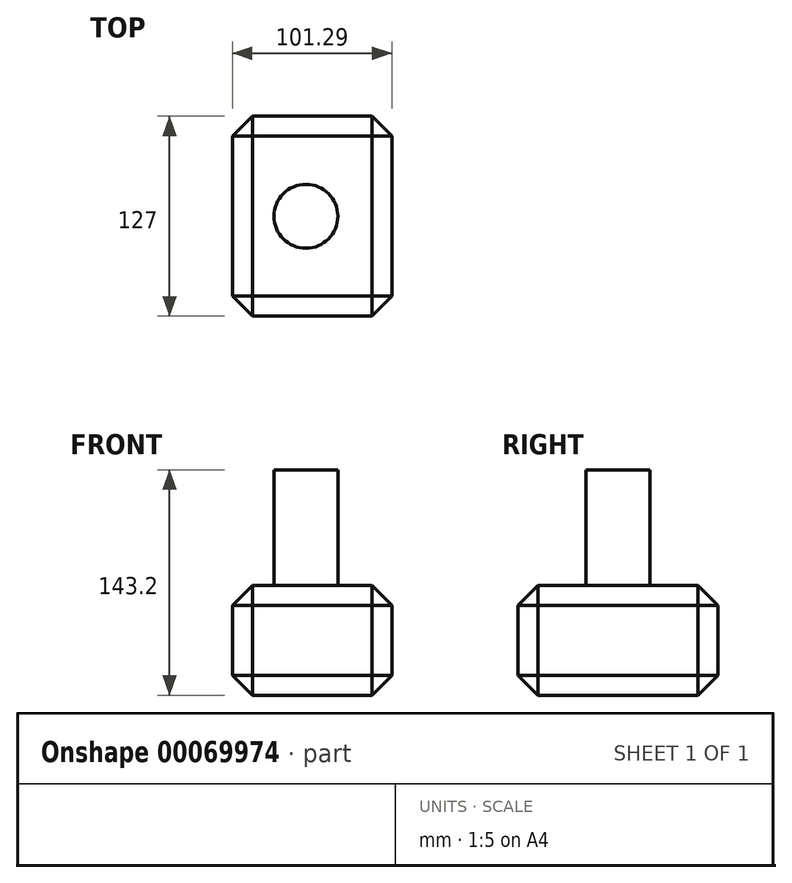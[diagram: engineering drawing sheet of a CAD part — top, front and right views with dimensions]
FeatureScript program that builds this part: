
annotation { "Feature Type Name" : "Feature", "Feature Type Description" : "" }
export const myFeature = defineFeature(function(context is Context, id is Id, definition is map)
    precondition{}
    {
        {
            var Q0;
            Q0=qCreatedBy(makeId("Front.planeOp"),FACE);
            var sketch = newSketch(context, id + "F0", { "sketchPlane" : qUnion([Q0])});
            skLineSegment(sketch, "E0.bottom", {"start": v(-46.67, 29.5) * mm, "end": v(54.62, 29.5) * mm});
            skLineSegment(sketch, "E0.top", {"start": v(-46.67, -40.29) * mm, "end": v(54.62, -40.29) * mm});
            skLineSegment(sketch, "E0.left", {"start": v(-46.67, 29.5) * mm, "end": v(-46.67, -40.29) * mm});
            skLineSegment(sketch, "E0.right", {"start": v(54.62, 29.5) * mm, "end": v(54.62, -40.29) * mm});
            skLineSegment(sketch, "E1.bottom", {"start": v(-58.3, 0) * mm, "end": v(-64.26, 0) * mm});
            skLineSegment(sketch, "E1.top", {"start": v(-58.3, 20.14) * mm, "end": v(-64.26, 20.14) * mm});
            skLineSegment(sketch, "E1.left", {"start": v(-58.3, 0) * mm, "end": v(-58.3, 20.14) * mm});
            skLineSegment(sketch, "E1.right", {"start": v(-64.26, 0) * mm, "end": v(-64.26, 20.14) * mm});
            skSolve(sketch);
        }
        {
            var Q0;
            Q0=makeQuery(id+"F0.imprint","IMPRINT",FACE,{"disambiguationData":[TD([[makeQuery(id+"F0.imprint","IMPRINT",EDGE,{"derivedFrom":sQuery(id+"F0.wireOp",EDGE,"E0.bottom")}),-1.0]])]});
            extrude(context, id + "F1", {"entities" : qUnion([Q0]), "endBound" : BoundingType.SYMMETRIC, "depth" : 127 * mm});
        }
        {
            var Q0;
            Q0=makeQuery(id+"F1.opExtrude","CAP_EDGE",EDGE,{"disambiguationData":[OSD([sQuery(id+"F0.wireOp",EDGE,"E0.bottom")])],"isStart":false});
            var Q1;
            Q1=makeQuery(id+"F1.opExtrude","SWEPT_EDGE",EDGE,{"disambiguationData":[OSD([sQuery(id+"F0.wireOp",EDGE,"E0.bottom"),sQuery(id+"F0.wireOp",EDGE,"E0.right")])]});
            var Q2;
            Q2=makeQuery(id+"F1.opExtrude","CAP_EDGE",EDGE,{"disambiguationData":[OSD([sQuery(id+"F0.wireOp",EDGE,"E0.bottom")])],"isStart":true});
            var Q3;
            Q3=makeQuery(id+"F1.opExtrude","SWEPT_EDGE",EDGE,{"disambiguationData":[OSD([sQuery(id+"F0.wireOp",EDGE,"E0.bottom"),sQuery(id+"F0.wireOp",EDGE,"E0.left")])]});
            var Q4;
            Q4=makeQuery(id+"F1.opExtrude","CAP_EDGE",EDGE,{"disambiguationData":[OSD([sQuery(id+"F0.wireOp",EDGE,"E0.right")])],"isStart":false});
            var Q5;
            Q5=makeQuery(id+"F1.opExtrude","CAP_EDGE",EDGE,{"disambiguationData":[OSD([sQuery(id+"F0.wireOp",EDGE,"E0.right")])],"isStart":true});
            var Q6;
            Q6=makeQuery(id+"F1.opExtrude","CAP_EDGE",EDGE,{"disambiguationData":[OSD([sQuery(id+"F0.wireOp",EDGE,"E0.left")])],"isStart":false});
            var Q7;
            Q7=makeQuery(id+"F1.opExtrude","CAP_EDGE",EDGE,{"disambiguationData":[OSD([sQuery(id+"F0.wireOp",EDGE,"E0.left")])],"isStart":true});
            var Q8;
            Q8=makeQuery(id+"F1.opExtrude","CAP_EDGE",EDGE,{"disambiguationData":[OSD([sQuery(id+"F0.wireOp",EDGE,"E0.top")])],"isStart":true});
            var Q9;
            Q9=makeQuery(id+"F1.opExtrude","SWEPT_EDGE",EDGE,{"disambiguationData":[OSD([sQuery(id+"F0.wireOp",EDGE,"E0.top"),sQuery(id+"F0.wireOp",EDGE,"E0.left")])]});
            var Q10;
            Q10=makeQuery(id+"F1.opExtrude","CAP_EDGE",EDGE,{"disambiguationData":[OSD([sQuery(id+"F0.wireOp",EDGE,"E0.top")])],"isStart":false});
            var Q11;
            Q11=makeQuery(id+"F1.opExtrude","SWEPT_EDGE",EDGE,{"disambiguationData":[OSD([sQuery(id+"F0.wireOp",EDGE,"E0.top"),sQuery(id+"F0.wireOp",EDGE,"E0.right")])]});
            chamfer(context, id + "F2", {"entities" : qUnion([Q0, Q1, Q2, Q3, Q4, Q5, Q6, Q7, Q8, Q9, Q10, Q11]), "width" : 12.7 * mm, "tangentPropagation" : true});
        }
        {
            var Q0;
            Q0=makeQuery(id+"F1.opExtrude","SWEPT_FACE",FACE,{"disambiguationData":[OSD([sQuery(id+"F0.wireOp",EDGE,"E0.bottom")])]});
            var sketch = newSketch(context, id + "F3", { "sketchPlane" : qUnion([Q0])});
            skCircle(sketch, "E2", {"center": v(0, 0) * mm, "radius": 20.3 * mm});
            skSolve(sketch);
        }
        {
            var Q0;
            Q0=makeQuery(id+"F3.imprint","IMPRINT",FACE,{"disambiguationData":[TD([[makeQuery(id+"F3.imprint","IMPRINT",EDGE,{"derivedFrom":sQuery(id+"F3.wireOp",EDGE,"E2")}),1.0]])]});
            extrude(context, id + "F4", {"entities" : qUnion([Q0]), "operationType" : NewBodyOperationType.ADD, "depth" : 73.4 * mm, "offsetDistance" : 25.4 * mm});
        }
    });
